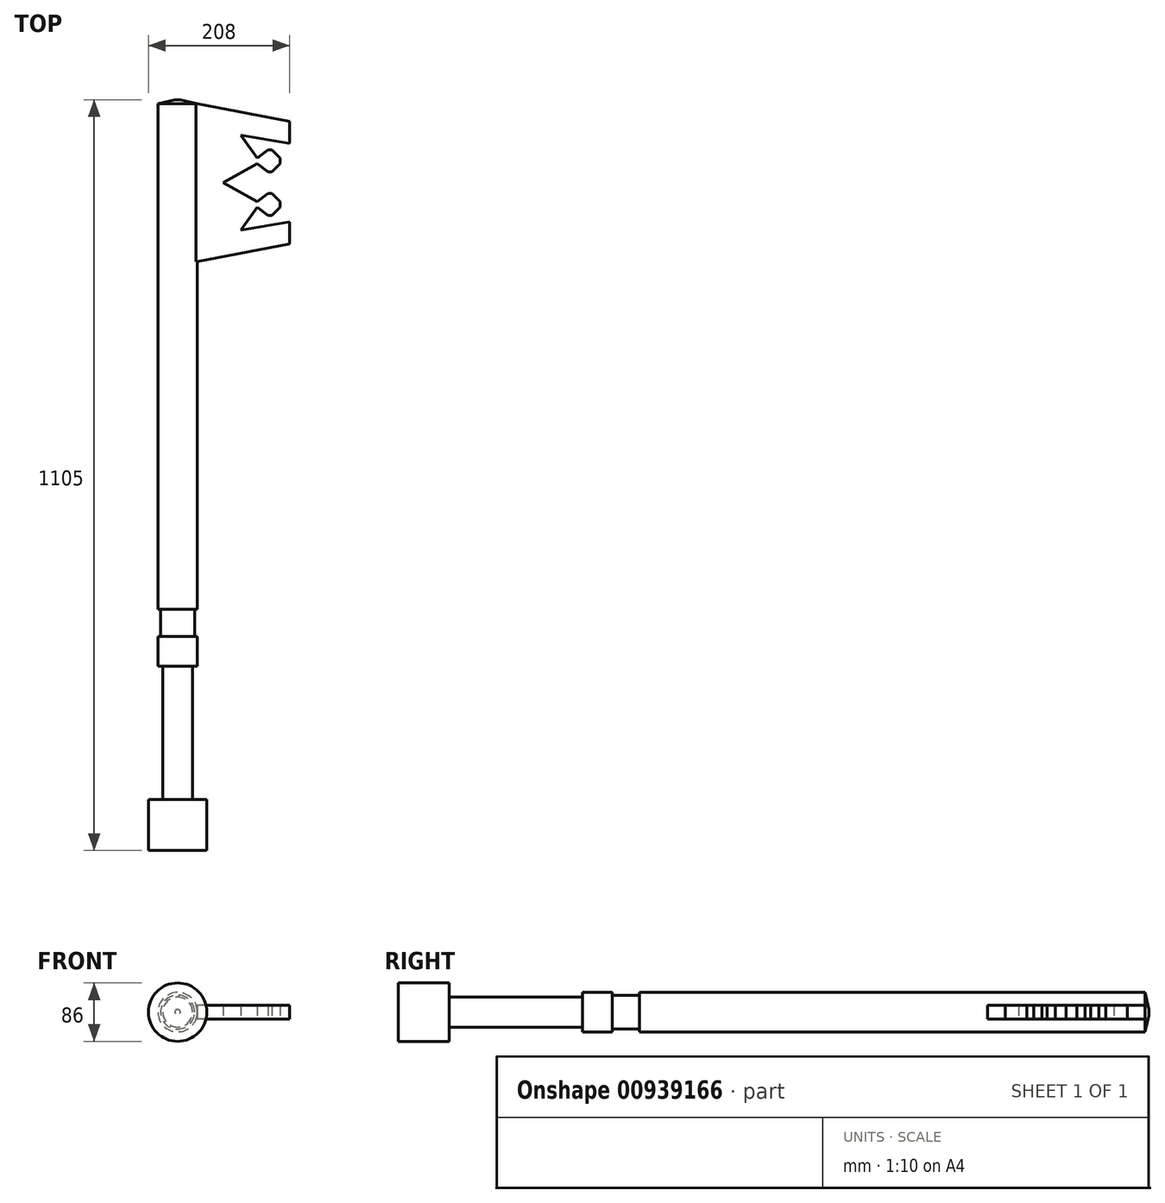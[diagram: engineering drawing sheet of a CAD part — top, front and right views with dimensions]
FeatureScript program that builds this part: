
annotation { "Feature Type Name" : "Feature", "Feature Type Description" : "" }
export const myFeature = defineFeature(function(context is Context, id is Id, definition is map)
    precondition{}
    {
        {
            var Q0;
            Q0=qCreatedBy(makeId("Front.planeOp"),FACE);
            var sketch = newSketch(context, id + "F0", { "sketchPlane" : qUnion([Q0])});
            skCircle(sketch, "E0", {"center": v(0, 0) * mm, "radius": 29 * mm});
            skSolve(sketch);
        }
        {
            var Q0;
            Q0=makeQuery(id+"F0.imprint","IMPRINT",FACE,{"disambiguationData":[TD([[makeQuery(id+"F0.imprint","IMPRINT",EDGE,{"derivedFrom":sQuery(id+"F0.wireOp",EDGE,"E0")}),1.0]])]});
            var Q1;
            Q1 = qSketchRegion(id + "F2", true);
            extrude(context, id + "F1", {"entities" : qUnion([Q0, Q1]), "oppositeDirection" : true, "depth" : 750 * mm, "offsetDistance" : 25 * mm});
        }
        {
            var Q0;
            Q0=qCreatedBy(makeId("Front.planeOp"),FACE);
            var sketch = newSketch(context, id + "F2", { "sketchPlane" : qUnion([Q0])});
            skCircle(sketch, "E1", {"center": v(0, 0) * mm, "radius": 25 * mm});
            skSolve(sketch);
        }
        {
            var Q0;
            Q0=makeQuery(id+"F2.imprint","IMPRINT",FACE,{"disambiguationData":[TD([[makeQuery(id+"F2.imprint","IMPRINT",EDGE,{"derivedFrom":sQuery(id+"F2.wireOp",EDGE,"E1")}),1.0]])]});
            extrude(context, id + "F3", {"entities" : qUnion([Q0]), "operationType" : NewBodyOperationType.ADD, "depth" : 40 * mm, "offsetDistance" : 25 * mm});
        }
        {
            var Q0;
            Q0=makeQuery(id+"F3.opExtrude","CAP_FACE",FACE,{"disambiguationData":[OSD([sQuery(id+"F2.wireOp",EDGE,"E1")])],"isStart":false});
            var sketch = newSketch(context, id + "F4", { "sketchPlane" : qUnion([Q0])});
            skCircle(sketch, "E2", {"center": v(0, 0) * mm, "radius": 29 * mm});
            skSolve(sketch);
        }
        {
            var Q0;
            Q0=makeQuery(id+"F4.imprint","IMPRINT",FACE,{"disambiguationData":[TD([[makeQuery(id+"F4.imprint","IMPRINT",EDGE,{"derivedFrom":sQuery(id+"F4.wireOp",EDGE,"E2")}),1.0]])]});
            var Q1;
            Q1=makeQuery(id+"F4.imprint","IMPRINT",FACE,{"disambiguationData":[TD([[makeQuery(id+"F4.imprint","IMPRINT",EDGE,{"derivedFrom":makeQuery(id+"F3.opExtrude","CAP_EDGE",EDGE,{"disambiguationData":[OSD([sQuery(id+"F2.wireOp",EDGE,"E1")])],"isStart":false})}),1.0]])]});
            var Q2;
            Q2=sQuery(id+"F4.wireOp",EDGE,"E2");
            extrude(context, id + "F5", {"entities" : qUnion([Q0, Q1]), "operationType" : NewBodyOperationType.ADD, "surfaceEntities" : qUnion([Q2]), "depth" : 44 * mm, "offsetDistance" : 25 * mm});
        }
        {
            var Q0;
            Q0=makeQuery(id+"F5.opExtrude","CAP_FACE",FACE,{"disambiguationData":[OSD([sQuery(id+"F4.wireOp",EDGE,"E2")])],"isStart":false});
            var sketch = newSketch(context, id + "F6", { "sketchPlane" : qUnion([Q0])});
            skCircle(sketch, "E3", {"center": v(0, 0) * mm, "radius": 22 * mm});
            skSolve(sketch);
        }
        {
            var Q0;
            Q0=makeQuery(id+"F6.imprint","IMPRINT",FACE,{"disambiguationData":[TD([[makeQuery(id+"F6.imprint","IMPRINT",EDGE,{"derivedFrom":sQuery(id+"F6.wireOp",EDGE,"E3")}),1.0]])]});
            extrude(context, id + "F7", {"entities" : qUnion([Q0]), "operationType" : NewBodyOperationType.ADD, "depth" : 196 * mm, "offsetDistance" : 25 * mm});
        }
        {
            var Q0;
            Q0=makeQuery(id+"F7.opExtrude","CAP_FACE",FACE,{"disambiguationData":[OSD([sQuery(id+"F6.wireOp",EDGE,"E3")])],"isStart":false});
            var sketch = newSketch(context, id + "F8", { "sketchPlane" : qUnion([Q0])});
            skCircle(sketch, "E4", {"center": v(0, 0) * mm, "radius": 43 * mm});
            skSolve(sketch);
        }
        {
            var Q0;
            Q0=makeQuery(id+"F8.imprint","IMPRINT",FACE,{"disambiguationData":[TD([[makeQuery(id+"F8.imprint","IMPRINT",EDGE,{"derivedFrom":sQuery(id+"F8.wireOp",EDGE,"E4")}),1.0]])]});
            var Q1;
            Q1=makeQuery(id+"F8.imprint","IMPRINT",FACE,{"disambiguationData":[TD([[makeQuery(id+"F8.imprint","IMPRINT",EDGE,{"derivedFrom":makeQuery(id+"F7.opExtrude","CAP_EDGE",EDGE,{"disambiguationData":[OSD([sQuery(id+"F6.wireOp",EDGE,"E3")])],"isStart":false})}),1.0]])]});
            extrude(context, id + "F9", {"entities" : qUnion([Q0, Q1]), "operationType" : NewBodyOperationType.ADD, "depth" : 75 * mm, "offsetDistance" : 25 * mm});
        }
        {
            var Q0;
            Q0=makeQuery(id+"F1.opExtrude","CAP_EDGE",EDGE,{"disambiguationData":[OSD([sQuery(id+"F0.wireOp",EDGE,"E0")])],"isStart":false});
            chamfer(context, id + "F10", {"entities" : qUnion([Q0]), "chamferType" : ChamferType.TWO_OFFSETS, "width1" : 6 * mm, "oppositeDirection" : false, "width2" : 25 * mm, "tangentPropagation" : true});
        }
        {
            var Q0;
            Q0=qCreatedBy(makeId("Top.planeOp"),FACE);
            var sketch = newSketch(context, id + "F11", { "sketchPlane" : qUnion([Q0])});
            skLineSegment(sketch, "E5", {"start": v(29, 744) * mm, "end": v(29, 512) * mm});
            skLineSegment(sketch, "E6", {"start": v(29, 512) * mm, "end": v(29, 538) * mm});
            skLineSegment(sketch, "E7", {"start": v(29, 538) * mm, "end": v(165, 538) * mm});
            skLineSegment(sketch, "E8", {"start": v(165, 538) * mm, "end": v(29, 512) * mm});
            skLineSegment(sketch, "E9", {"start": v(29, 744) * mm, "end": v(29, 718) * mm});
            skLineSegment(sketch, "E10", {"start": v(29, 718) * mm, "end": v(165, 718) * mm});
            skLineSegment(sketch, "E11", {"start": v(165, 718) * mm, "end": v(29, 744) * mm});
            skLineSegment(sketch, "E12", {"start": v(165, 718) * mm, "end": v(165, 686) * mm});
            skLineSegment(sketch, "E13", {"start": v(165, 686) * mm, "end": v(165, 698) * mm});
            skLineSegment(sketch, "E14", {"start": v(165, 698) * mm, "end": v(93, 698) * mm});
            skLineSegment(sketch, "E15", {"start": v(93, 698) * mm, "end": v(165, 686) * mm});
            skLineSegment(sketch, "E16", {"start": v(93, 698) * mm, "end": v(93, 664) * mm});
            skLineSegment(sketch, "E17", {"start": v(93, 664) * mm, "end": v(117, 664) * mm});
            skLineSegment(sketch, "E18", {"start": v(117, 664) * mm, "end": v(93, 698) * mm});
            skLineSegment(sketch, "E19", {"start": v(117, 664) * mm, "end": v(133, 664) * mm});
            skLineSegment(sketch, "E20", {"start": v(133, 664) * mm, "end": v(133, 676) * mm});
            skLineSegment(sketch, "E21", {"start": v(133, 676) * mm, "end": v(117, 664) * mm});
            skLineSegment(sketch, "E22", {"start": v(133, 676) * mm, "end": v(139, 676) * mm});
            skLineSegment(sketch, "E23", {"start": v(133, 664) * mm, "end": v(139, 664) * mm});
            skLineSegment(sketch, "E24", {"start": v(139, 664) * mm, "end": v(139, 676) * mm});
            skLineSegment(sketch, "E25", {"start": v(139, 676) * mm, "end": v(139, 664) * mm});
            skLineSegment(sketch, "E26", {"start": v(139, 664) * mm, "end": v(151, 664) * mm});
            skLineSegment(sketch, "E27", {"start": v(151, 664) * mm, "end": v(139, 676) * mm});
            skLineSegment(sketch, "E28", {"start": v(151, 664) * mm, "end": v(151, 656) * mm});
            skLineSegment(sketch, "E29", {"start": v(93, 664) * mm, "end": v(93, 656) * mm});
            skLineSegment(sketch, "E30", {"start": v(93, 656) * mm, "end": v(151, 656) * mm});
            skLineSegment(sketch, "E31", {"start": v(151, 656) * mm, "end": v(139, 656) * mm});
            skLineSegment(sketch, "E32", {"start": v(139, 656) * mm, "end": v(139, 644) * mm});
            skLineSegment(sketch, "E33", {"start": v(139, 644) * mm, "end": v(151, 656) * mm});
            skLineSegment(sketch, "E34", {"start": v(139, 644) * mm, "end": v(133, 644) * mm});
            skLineSegment(sketch, "E35", {"start": v(139, 656) * mm, "end": v(133, 656) * mm});
            skLineSegment(sketch, "E36", {"start": v(133, 656) * mm, "end": v(133, 644) * mm});
            skLineSegment(sketch, "E37", {"start": v(133, 656) * mm, "end": v(117, 656) * mm});
            skLineSegment(sketch, "E38", {"start": v(117, 656) * mm, "end": v(133, 644) * mm});
            skLineSegment(sketch, "E39", {"start": v(117, 656) * mm, "end": v(67, 656) * mm});
            skLineSegment(sketch, "E40", {"start": v(67, 656) * mm, "end": v(67, 628) * mm});
            skLineSegment(sketch, "E41", {"start": v(67, 628) * mm, "end": v(117, 656) * mm});
            skLineSegment(sketch, "E42", {"start": v(67, 628) * mm, "end": v(67, 600) * mm});
            skLineSegment(sketch, "E43", {"start": v(67, 600) * mm, "end": v(117, 600) * mm});
            skLineSegment(sketch, "E44", {"start": v(117, 600) * mm, "end": v(67, 628) * mm});
            skLineSegment(sketch, "E45", {"start": v(117, 600) * mm, "end": v(133, 600) * mm});
            skLineSegment(sketch, "E46", {"start": v(133, 600) * mm, "end": v(133, 612) * mm});
            skLineSegment(sketch, "E47", {"start": v(133, 612) * mm, "end": v(117, 600) * mm});
            skLineSegment(sketch, "E48", {"start": v(133, 612) * mm, "end": v(139, 612) * mm});
            skLineSegment(sketch, "E49", {"start": v(133, 600) * mm, "end": v(139, 600) * mm});
            skLineSegment(sketch, "E50", {"start": v(139, 600) * mm, "end": v(139, 612) * mm});
            skLineSegment(sketch, "E51", {"start": v(139, 600) * mm, "end": v(151, 600) * mm});
            skLineSegment(sketch, "E52", {"start": v(151, 600) * mm, "end": v(139, 612) * mm});
            skLineSegment(sketch, "E53", {"start": v(151, 600) * mm, "end": v(151, 592) * mm});
            skLineSegment(sketch, "E54", {"start": v(67, 600) * mm, "end": v(67, 592) * mm});
            skLineSegment(sketch, "E55", {"start": v(67, 592) * mm, "end": v(151, 592) * mm});
            skLineSegment(sketch, "E56", {"start": v(151, 592) * mm, "end": v(139, 592) * mm});
            skLineSegment(sketch, "E57", {"start": v(139, 592) * mm, "end": v(139, 580) * mm});
            skLineSegment(sketch, "E58", {"start": v(139, 580) * mm, "end": v(151, 592) * mm});
            skLineSegment(sketch, "E59", {"start": v(139, 580) * mm, "end": v(133, 580) * mm});
            skLineSegment(sketch, "E60", {"start": v(139, 592) * mm, "end": v(133, 592) * mm});
            skLineSegment(sketch, "E61", {"start": v(133, 592) * mm, "end": v(133, 580) * mm});
            skLineSegment(sketch, "E62", {"start": v(133, 592) * mm, "end": v(117, 592) * mm});
            skLineSegment(sketch, "E63", {"start": v(117, 592) * mm, "end": v(133, 580) * mm});
            skLineSegment(sketch, "E64", {"start": v(165, 538) * mm, "end": v(165, 570) * mm});
            skLineSegment(sketch, "E65", {"start": v(165, 570) * mm, "end": v(165, 558) * mm});
            skLineSegment(sketch, "E66", {"start": v(165, 558) * mm, "end": v(93, 558) * mm});
            skLineSegment(sketch, "E67", {"start": v(93, 558) * mm, "end": v(165, 570) * mm});
            skLineSegment(sketch, "E68", {"start": v(93, 558) * mm, "end": v(93, 592) * mm});
            skLineSegment(sketch, "E69", {"start": v(93, 592) * mm, "end": v(117, 592) * mm});
            skLineSegment(sketch, "E70", {"start": v(117, 592) * mm, "end": v(93, 558) * mm});
            skLineSegment(sketch, "E71", {"start": v(29, 718) * mm, "end": v(29, 538) * mm});
            skLineSegment(sketch, "E72", {"start": v(4, 512) * mm, "end": v(29, 512) * mm});
            skLineSegment(sketch, "E73", {"start": v(4, 512) * mm, "end": v(4, 744) * mm});
            skLineSegment(sketch, "E74", {"start": v(4, 744) * mm, "end": v(29, 744) * mm});
            skSolve(sketch);
        }
        {
            var Q0;
            Q0 = qSketchRegion(id + "F11", true);
            extrude(context, id + "F12", {"entities" : qUnion([Q0]), "operationType" : NewBodyOperationType.ADD, "endBound" : BoundingType.SYMMETRIC, "depth" : 20 * mm, "offsetDistance" : 25 * mm});
        }
    });
